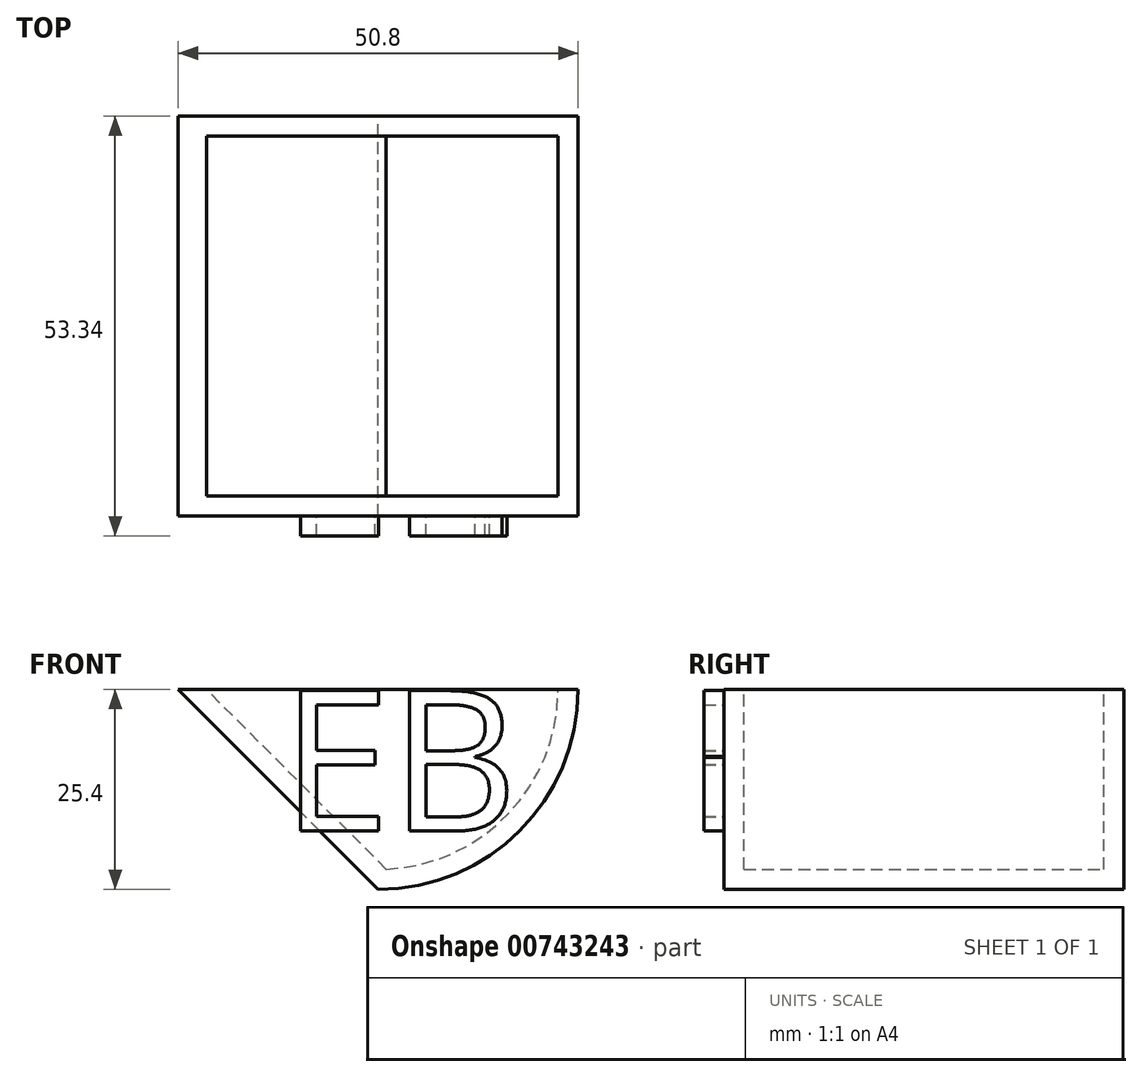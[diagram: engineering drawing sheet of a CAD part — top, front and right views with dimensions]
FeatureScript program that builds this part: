
annotation { "Feature Type Name" : "Feature", "Feature Type Description" : "" }
export const myFeature = defineFeature(function(context is Context, id is Id, definition is map)
    precondition{}
    {
        {
            var Q0;
            Q0=qCreatedBy(makeId("Front.planeOp"),FACE);
            var sketch = newSketch(context, id + "F0", { "sketchPlane" : qUnion([Q0])});
            skLineSegment(sketch, "E0.bottom", {"start": v(-50.8, 1.6) * mm, "end": v(0, 1.6) * mm});
            skLineSegment(sketch, "E1", {"start": v(-25.4, -23.8) * mm, "end": v(-50.8, 1.6) * mm});
            skArc(sketch, "E2", {"start": v(-25.4, -23.8) * mm, "mid": v(-7.44, -16.36) * mm, "end": v(0, 1.6) * mm});
            skPoint(sketch, "E3.orphan", {"position": v(-50.8, -23.8) * mm});
            skPoint(sketch, "E0.right.end.orphan", {"position": v(0, -23.8) * mm});
            skSolve(sketch);
        }
        {
            var Q0;
            Q0=makeQuery(id+"F0.imprint","IMPRINT",FACE,{"disambiguationData":[TD([[makeQuery(id+"F0.imprint","IMPRINT",EDGE,{"derivedFrom":sQuery(id+"F0.wireOp",EDGE,"E0.bottom")}),-1.0]])]});
            extrude(context, id + "F1", {"entities" : qUnion([Q0]), "depth" : 50.8 * mm, "offsetDistance" : 25.4 * mm});
        }
        {
            var Q0;
            Q0=makeQuery(id+"F1.opExtrude","SWEPT_FACE",FACE,{"disambiguationData":[OSD([sQuery(id+"F0.wireOp",EDGE,"E0.bottom")])]});
            shell(context, id + "F2", {"entities" : qUnion([Q0]), "thickness" : 2.54 * mm});
        }
        {
            var Q0;
            Q0=makeQuery(id+"F1.opExtrude","CAP_FACE",FACE,{"disambiguationData":[OSD([sQuery(id+"F0.wireOp",EDGE,"E0.bottom"),sQuery(id+"F0.wireOp",EDGE,"E1"),sQuery(id+"F0.wireOp",EDGE,"E2")])],"isStart":false});
            var sketch = newSketch(context, id + "F3", { "sketchPlane" : qUnion([Q0])});
            skText(sketch, "E4", { "text": "EB", "fontName": "OpenSans-Regular.ttf"});
            const initialGuessF3  = {"E4": [-0.03772, -0.01636, 1, 0, 0.01796]};
            skSetInitialGuess(sketch, initialGuessF3);
            skSolve(sketch);
        }
        {
            var Q0;
            Q0 = qSketchRegion(id + "F3", true);
            extrude(context, id + "F4", {"entities" : qUnion([Q0]), "operationType" : NewBodyOperationType.ADD, "depth" : 2.54 * mm, "offsetDistance" : 25.4 * mm});
        }
    });
